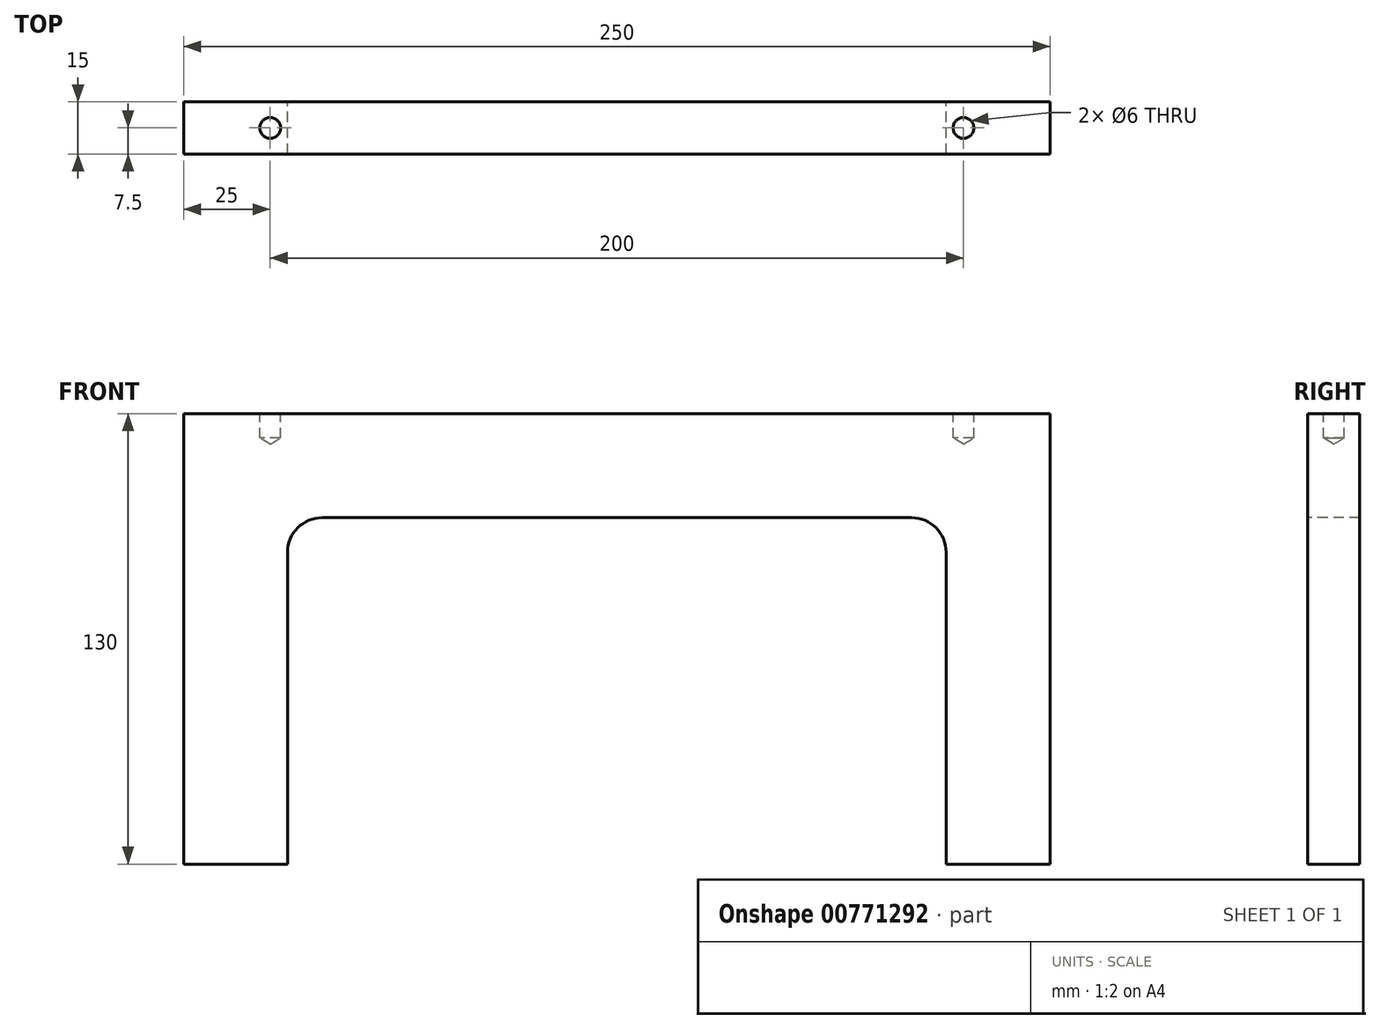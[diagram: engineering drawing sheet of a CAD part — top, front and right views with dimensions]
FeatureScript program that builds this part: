
annotation { "Feature Type Name" : "Feature", "Feature Type Description" : "" }
export const myFeature = defineFeature(function(context is Context, id is Id, definition is map)
    precondition{}
    {
        {
            var Q0;
            Q0=qCreatedBy(makeId("Top.planeOp"),FACE);
            var sketch = newSketch(context, id + "F0", { "sketchPlane" : qUnion([Q0])});
            skLineSegment(sketch, "E0.bottom", {"start": v(125, -7.5) * mm, "end": v(-125, -7.5) * mm});
            skLineSegment(sketch, "E0.top", {"start": v(125, 7.5) * mm, "end": v(-125, 7.5) * mm});
            skLineSegment(sketch, "E0.left", {"start": v(125, -7.5) * mm, "end": v(125, 7.5) * mm});
            skLineSegment(sketch, "E0.right", {"start": v(-125, -7.5) * mm, "end": v(-125, 7.5) * mm});
            skPoint(sketch, "E0.middle", {"position": v(0, 0) * mm});
            skPoint(sketch, "E1", {"position": v(-100, 0) * mm});
            skPoint(sketch, "E2", {"position": v(100, 0) * mm});
            skSolve(sketch);
        }
        {
            var Q0;
            Q0=makeQuery(id+"F0.imprint","IMPRINT",FACE,{"disambiguationData":[TD([[makeQuery(id+"F0.imprint","IMPRINT",EDGE,{"derivedFrom":sQuery(id+"F0.wireOp",EDGE,"E0.bottom")}),-1.0]])]});
            extrude(context, id + "F1", {"entities" : qUnion([Q0]), "oppositeDirection" : true, "depth" : 130 * mm, "offsetDistance" : 25 * mm});
        }
        {
            var Q0;
            Q0=sQuery(id+"F0.wireOp",VERTEX,"E1");
            var Q1;
            Q1=sQuery(id+"F0.wireOp",VERTEX,"E2");
            var Q2;
            Q2=makeQuery(id+"F1.opExtrude","SWEPT_BODY",BODY,{"disambiguationData":[OSD([sQuery(id+"F0.wireOp",EDGE,"E0.bottom"),sQuery(id+"F0.wireOp",EDGE,"E0.top"),sQuery(id+"F0.wireOp",EDGE,"E0.left"),sQuery(id+"F0.wireOp",EDGE,"E0.right")])]});
            hole(context, id + "F2", {"style" : HoleStyle.SIMPLE, "endStyle" : HoleEndStyle.BLIND, "holeDiameter" : 6 * mm, "majorDiameter" : 5 * mm, "holeDepth" : 7 * mm, "isTappedThrough" : true, "tappedDepth" : 12 * mm, "tapClearance" : 3, "locations" : qUnion([Q0, Q1]), "scope" : qUnion([Q2])});
        }
        {
            var Q0;
            Q0=qCreatedBy(makeId("Front.planeOp"),FACE);
            var sketch = newSketch(context, id + "F3", { "sketchPlane" : qUnion([Q0])});
            skLineSegment(sketch, "E3.bottom", {"start": v(95, -177.2) * mm, "end": v(-95, -177.2) * mm});
            skLineSegment(sketch, "E3.top", {"start": v(85, -30) * mm, "end": v(-85, -30) * mm});
            skLineSegment(sketch, "E3.left", {"start": v(95, -177.2) * mm, "end": v(95, -40) * mm});
            skLineSegment(sketch, "E3.right", {"start": v(-95, -177.2) * mm, "end": v(-95, -40) * mm});
            skPoint(sketch, "E3.middle", {"position": v(0, -103.6) * mm});
            skPoint(sketch, "E4.visualSharp", {"position": v(-95, -30) * mm});
            skArc(sketch, "E4.filletArc", {"start": v(-85, -30) * mm, "mid": v(-92.07, -32.93) * mm, "end": v(-95, -40) * mm});
            skPoint(sketch, "E5.visualSharp", {"position": v(95, -30) * mm});
            skArc(sketch, "E5.filletArc", {"start": v(95, -40) * mm, "mid": v(92.07, -32.93) * mm, "end": v(85, -30) * mm});
            skSolve(sketch);
        }
        {
            var Q0;
            Q0=makeQuery(id+"F3.imprint","IMPRINT",FACE,{"disambiguationData":[TD([[makeQuery(id+"F3.imprint","IMPRINT",EDGE,{"derivedFrom":sQuery(id+"F3.wireOp",EDGE,"E3.bottom")}),-1.0]])]});
            extrude(context, id + "F4", {"entities" : qUnion([Q0]), "operationType" : NewBodyOperationType.REMOVE, "endBound" : BoundingType.SYMMETRIC, "oppositeDirection" : true, "depth" : 25 * mm, "offsetDistance" : 25 * mm});
        }
    });
